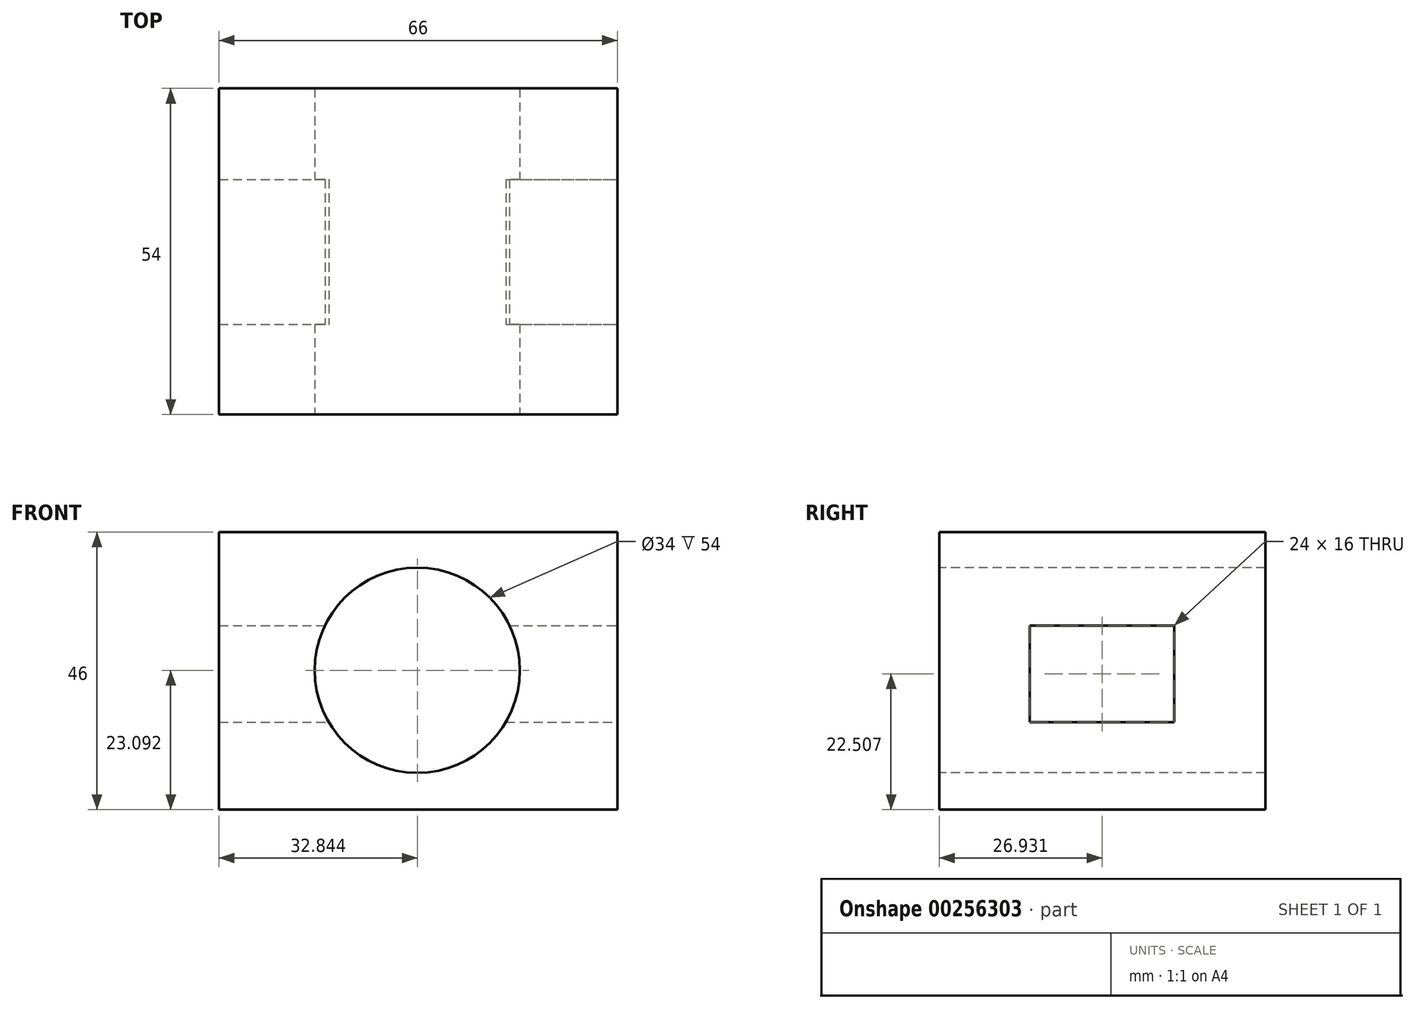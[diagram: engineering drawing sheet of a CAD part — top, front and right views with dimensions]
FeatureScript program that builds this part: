
annotation { "Feature Type Name" : "Feature", "Feature Type Description" : "" }
export const myFeature = defineFeature(function(context is Context, id is Id, definition is map)
    precondition{}
    {
        {
            var Q0;
            Q0=qCreatedBy(makeId("Top.planeOp"),FACE);
            var sketch = newSketch(context, id + "F0", { "sketchPlane" : qUnion([Q0])});
            skLineSegment(sketch, "E0.bottom", {"start": v(-21.15, 9) * mm, "end": v(44.85, 9) * mm});
            skLineSegment(sketch, "E0.top", {"start": v(-21.15, -45) * mm, "end": v(44.85, -45) * mm});
            skLineSegment(sketch, "E0.left", {"start": v(-21.15, 9) * mm, "end": v(-21.15, -45) * mm});
            skLineSegment(sketch, "E0.right", {"start": v(44.85, 9) * mm, "end": v(44.85, -45) * mm});
            skSolve(sketch);
        }
        {
            var Q0;
            Q0=makeQuery(id+"F0.imprint","IMPRINT",FACE,{"disambiguationData":[TD([[makeQuery(id+"F0.imprint","IMPRINT",EDGE,{"derivedFrom":sQuery(id+"F0.wireOp",EDGE,"E0.bottom")}),-1.0]])]});
            extrude(context, id + "F1", {"entities" : qUnion([Q0]), "depth" : 46 * mm});
        }
        {
            var Q0;
            Q0=makeQuery(id+"F1.opExtrude","SWEPT_FACE",FACE,{"disambiguationData":[OSD([sQuery(id+"F0.wireOp",EDGE,"E0.top")])]});
            var sketch = newSketch(context, id + "F2", { "sketchPlane" : qUnion([Q0])});
            skCircle(sketch, "E1", {"center": v(11.7, 23.1) * mm, "radius": 17 * mm});
            skSolve(sketch);
        }
        {
            var Q0;
            Q0=makeQuery(id+"F2.imprint","IMPRINT",FACE,{"disambiguationData":[TD([[makeQuery(id+"F2.imprint","IMPRINT",EDGE,{"derivedFrom":sQuery(id+"F2.wireOp",EDGE,"E1")}),1.0]])]});
            extrude(context, id + "F3", {"entities" : qUnion([Q0]), "operationType" : NewBodyOperationType.REMOVE, "oppositeDirection" : true, "depth" : 54 * mm});
        }
        {
            var Q0;
            Q0=makeQuery(id+"F1.opExtrude","SWEPT_FACE",FACE,{"disambiguationData":[OSD([sQuery(id+"F0.wireOp",EDGE,"E0.right")])]});
            var sketch = newSketch(context, id + "F4", { "sketchPlane" : qUnion([Q0])});
            skLineSegment(sketch, "E2.bottom", {"start": v(-30.07, 30.5) * mm, "end": v(-6.07, 30.5) * mm});
            skLineSegment(sketch, "E2.top", {"start": v(-30.07, 14.5) * mm, "end": v(-6.07, 14.5) * mm});
            skLineSegment(sketch, "E2.left", {"start": v(-30.07, 30.5) * mm, "end": v(-30.07, 14.5) * mm});
            skLineSegment(sketch, "E2.right", {"start": v(-6.07, 30.5) * mm, "end": v(-6.07, 14.5) * mm});
            skSolve(sketch);
        }
        {
            var Q0;
            Q0=makeQuery(id+"F4.imprint","IMPRINT",FACE,{"disambiguationData":[TD([[makeQuery(id+"F4.imprint","IMPRINT",EDGE,{"derivedFrom":sQuery(id+"F4.wireOp",EDGE,"E2.bottom")}),-1.0]])]});
            extrude(context, id + "F5", {"entities" : qUnion([Q0]), "operationType" : NewBodyOperationType.REMOVE, "oppositeDirection" : true, "depth" : 66 * mm});
        }
    });
